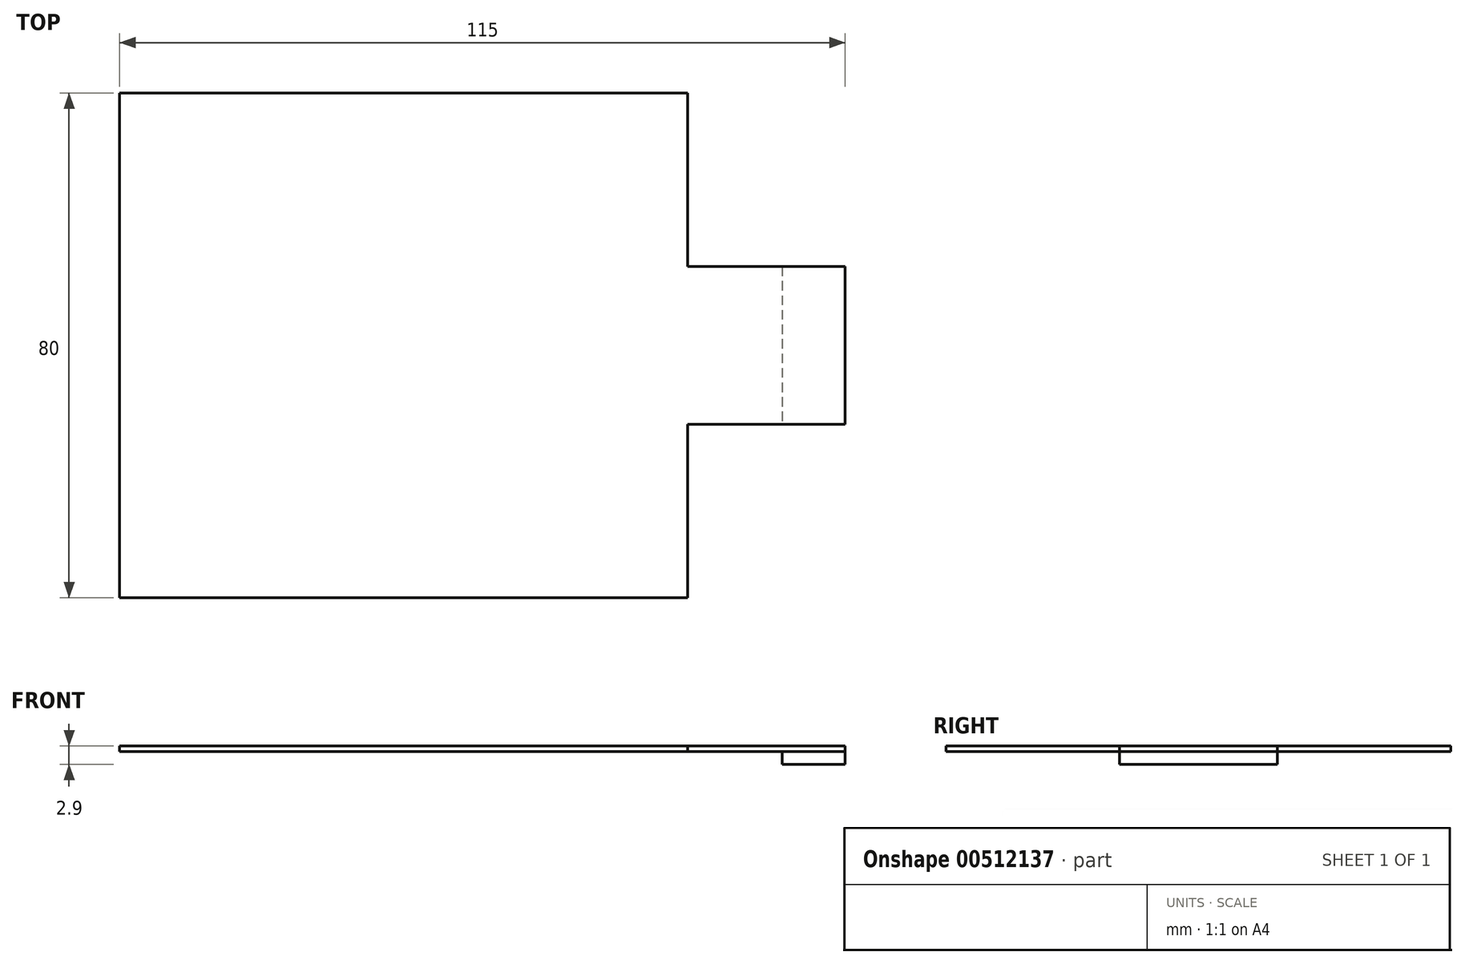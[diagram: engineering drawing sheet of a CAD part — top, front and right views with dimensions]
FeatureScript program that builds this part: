
annotation { "Feature Type Name" : "Feature", "Feature Type Description" : "" }
export const myFeature = defineFeature(function(context is Context, id is Id, definition is map)
    precondition{}
    {
        {
            var Q0;
            Q0=qCreatedBy(makeId("Top.planeOp"),FACE);
            var sketch = newSketch(context, id + "F0", { "sketchPlane" : qUnion([Q0])});
            skLineSegment(sketch, "E0.left", {"start": v(45, 40) * mm, "end": v(45, -40) * mm});
            skLineSegment(sketch, "E0.right", {"start": v(-45, 40) * mm, "end": v(-45, -40) * mm});
            skPoint(sketch, "E0.middle", {"position": v(0, 0) * mm});
            skLineSegment(sketch, "E1", {"start": v(-45, 40) * mm, "end": v(45, 40) * mm});
            skLineSegment(sketch, "E2", {"start": v(-45, -40) * mm, "end": v(45, -40) * mm});
            skLineSegment(sketch, "E3", {"start": v(0, 0) * mm, "end": v(70, 0) * mm, "construction": true});
            skLineSegment(sketch, "E4.bottom", {"start": v(60, 12.5) * mm, "end": v(70, 12.5) * mm});
            skLineSegment(sketch, "E4.top", {"start": v(60, -12.5) * mm, "end": v(70, -12.5) * mm});
            skLineSegment(sketch, "E4.left", {"start": v(60, 12.5) * mm, "end": v(60, -12.5) * mm});
            skLineSegment(sketch, "E4.right", {"start": v(70, 12.5) * mm, "end": v(70, -12.5) * mm});
            skLineSegment(sketch, "E5", {"start": v(60, 12.5) * mm, "end": v(45, 12.5) * mm});
            skLineSegment(sketch, "E6", {"start": v(60, -12.5) * mm, "end": v(45, -12.5) * mm});
            skSolve(sketch);
        }
        {
            var Q0;
            Q0=makeQuery(id+"F0.imprint","IMPRINT",FACE,{"disambiguationData":[TD([[makeQuery(id+"F0.imprint","IMPRINT",EDGE,{"derivedFrom":sQuery(id+"F0.wireOp",EDGE,"E0.left")}),-1.0]])]});
            var Q1;
            Q1=makeQuery(id+"F0.imprint","IMPRINT",FACE,{"disambiguationData":[TD([[makeQuery(id+"F0.imprint","IMPRINT",EDGE,{"derivedFrom":sQuery(id+"F0.wireOp",EDGE,"E4.left")}),-1.0]])]});
            var Q2;
            Q2=makeQuery(id+"F0.imprint","IMPRINT",FACE,{"disambiguationData":[TD([[makeQuery(id+"F0.imprint","IMPRINT",EDGE,{"derivedFrom":sQuery(id+"F0.wireOp",EDGE,"E4.bottom")}),-1.0]])]});
            extrude(context, id + "F1", {"entities" : qUnion([Q0, Q1, Q2]), "depth" : 0.9 * mm, "offsetDistance" : 25 * mm});
        }
        {
            var Q0;
            Q0=makeQuery(id+"F0.imprint","IMPRINT",FACE,{"disambiguationData":[TD([[makeQuery(id+"F0.imprint","IMPRINT",EDGE,{"derivedFrom":sQuery(id+"F0.wireOp",EDGE,"E4.bottom")}),-1.0]])]});
            extrude(context, id + "F2", {"entities" : qUnion([Q0]), "oppositeDirection" : true, "depth" : 2 * mm, "offsetDistance" : 25 * mm});
        }
    });
